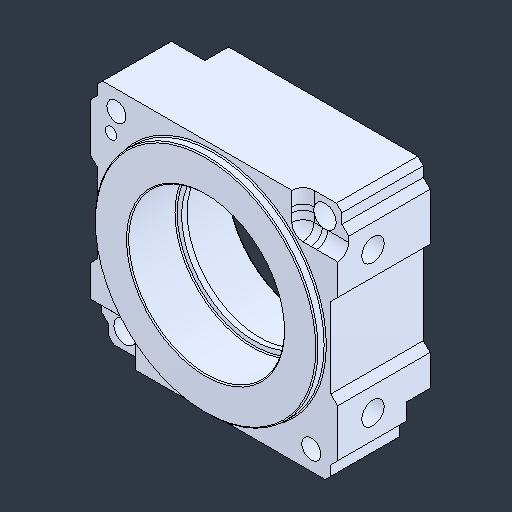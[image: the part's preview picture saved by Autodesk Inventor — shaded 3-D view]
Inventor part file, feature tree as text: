
AUTODESK INVENTOR PART (.ipt)
format: ipt  version: 2024.3 (Build 283343000, 343)  size: 225,792 bytes
history: native  units: in
note: dims shown in document units (in); Inventor stores cm internally (conversion verified against a paired STEP export)
features: chamfer x1
ambient origin geometry x8: Origin, YZ Plane, XZ Plane, XY Plane, X Axis, Y Axis, Z Axis, Center Point
bodies: Solid1 (feature_tree)
feature tree (1):
  chamfer  "Chamfer2"  [1 undecoded]
note: 1 required parameter value undecoded (feature->parameter linkage not recoverable at this tier; creation-order binding heuristic only, values carry confidence <= 0.55)
